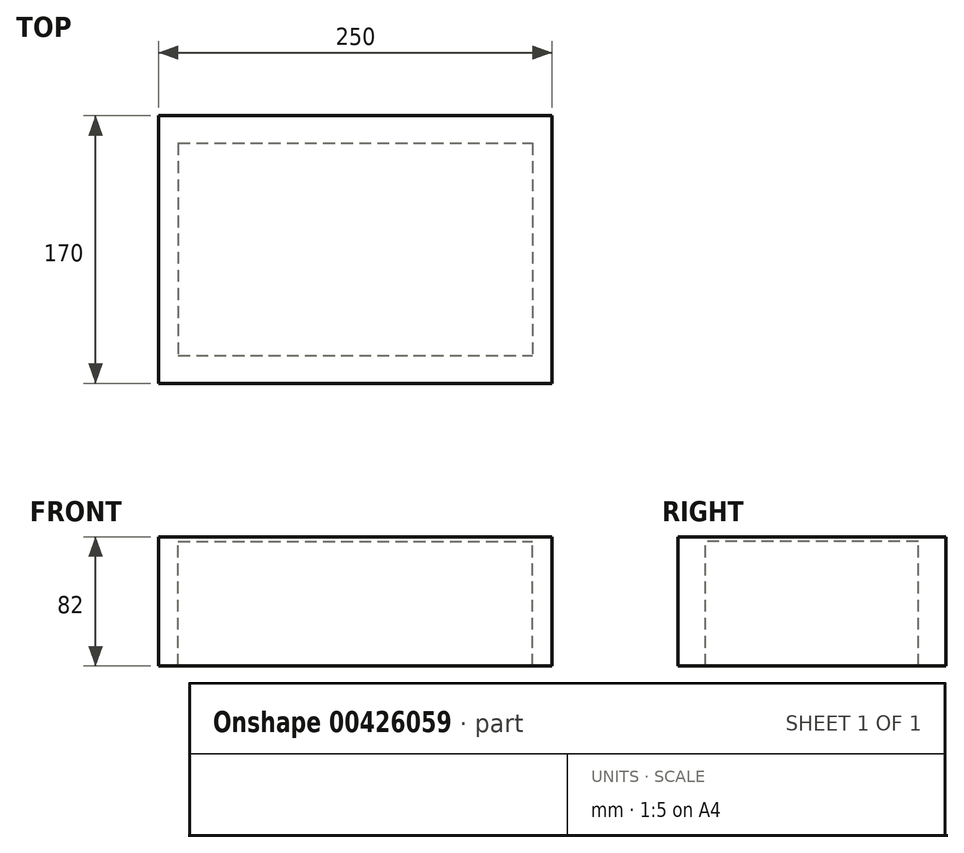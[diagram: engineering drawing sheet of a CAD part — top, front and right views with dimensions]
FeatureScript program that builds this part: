
annotation { "Feature Type Name" : "Feature", "Feature Type Description" : "" }
export const myFeature = defineFeature(function(context is Context, id is Id, definition is map)
    precondition{}
    {
        {
            var Q0;
            Q0=qCreatedBy(makeId("Top.planeOp"),FACE);
            var sketch = newSketch(context, id + "F0", { "sketchPlane" : qUnion([Q0])});
            skLineSegment(sketch, "E0.bottom", {"start": v(125, -85) * mm, "end": v(-125, -85) * mm});
            skLineSegment(sketch, "E0.top", {"start": v(125, 85) * mm, "end": v(-125, 85) * mm});
            skLineSegment(sketch, "E0.left", {"start": v(125, -85) * mm, "end": v(125, 85) * mm});
            skLineSegment(sketch, "E0.right", {"start": v(-125, -85) * mm, "end": v(-125, 85) * mm});
            skPoint(sketch, "E0.middle", {"position": v(0, 0) * mm});
            skLineSegment(sketch, "E1.bottom", {"start": v(117.5, -75) * mm, "end": v(-117.5, -75) * mm});
            skLineSegment(sketch, "E1.top", {"start": v(117.5, 75) * mm, "end": v(-117.5, 75) * mm});
            skLineSegment(sketch, "E1.left", {"start": v(117.5, -75) * mm, "end": v(117.5, 75) * mm});
            skLineSegment(sketch, "E1.right", {"start": v(-117.5, -75) * mm, "end": v(-117.5, 75) * mm});
            skSolve(sketch);
        }
        {
            var Q0;
            Q0=makeQuery(id+"F0.imprint","IMPRINT",FACE,{"disambiguationData":[TD([[makeQuery(id+"F0.imprint","IMPRINT",EDGE,{"derivedFrom":sQuery(id+"F0.wireOp",EDGE,"E1.bottom")}),-1.0]])]});
            var Q1;
            Q1=makeQuery(id+"F0.imprint","IMPRINT",FACE,{"disambiguationData":[TD([[makeQuery(id+"F0.imprint","IMPRINT",EDGE,{"derivedFrom":sQuery(id+"F0.wireOp",EDGE,"E0.bottom")}),-1.0]])]});
            extrude(context, id + "F1", {"entities" : qUnion([Q0, Q1]), "depth" : 3 * mm});
        }
        {
            var Q0;
            Q0=makeQuery(id+"F1.opExtrude","CAP_FACE",FACE,{"disambiguationData":[OSD([sQuery(id+"F0.wireOp",EDGE,"E0.bottom"),sQuery(id+"F0.wireOp",EDGE,"E0.top"),sQuery(id+"F0.wireOp",EDGE,"E0.left"),sQuery(id+"F0.wireOp",EDGE,"E0.right")])],"isStart":false});
            var sketch = newSketch(context, id + "F2", { "sketchPlane" : qUnion([Q0])});
            skLineSegment(sketch, "E2.bottom", {"start": v(-112.5, 67.5) * mm, "end": v(112.5, 67.5) * mm});
            skLineSegment(sketch, "E2.top", {"start": v(-112.5, -67.5) * mm, "end": v(112.5, -67.5) * mm});
            skLineSegment(sketch, "E2.left", {"start": v(-112.5, 67.5) * mm, "end": v(-112.5, -67.5) * mm});
            skLineSegment(sketch, "E2.right", {"start": v(112.5, 67.5) * mm, "end": v(112.5, -67.5) * mm});
            skPoint(sketch, "E2.middle", {"position": v(0, 0) * mm});
            skSolve(sketch);
        }
        {
            var Q0;
            Q0=makeQuery(id+"F2.imprint","IMPRINT",FACE,{"disambiguationData":[TD([[makeQuery(id+"F2.imprint","IMPRINT",EDGE,{"derivedFrom":sQuery(id+"F2.wireOp",EDGE,"E2.bottom")}),1.0]])]});
            extrude(context, id + "F3", {"entities" : qUnion([Q0]), "operationType" : NewBodyOperationType.ADD, "oppositeDirection" : true, "depth" : 82 * mm});
        }
    });
